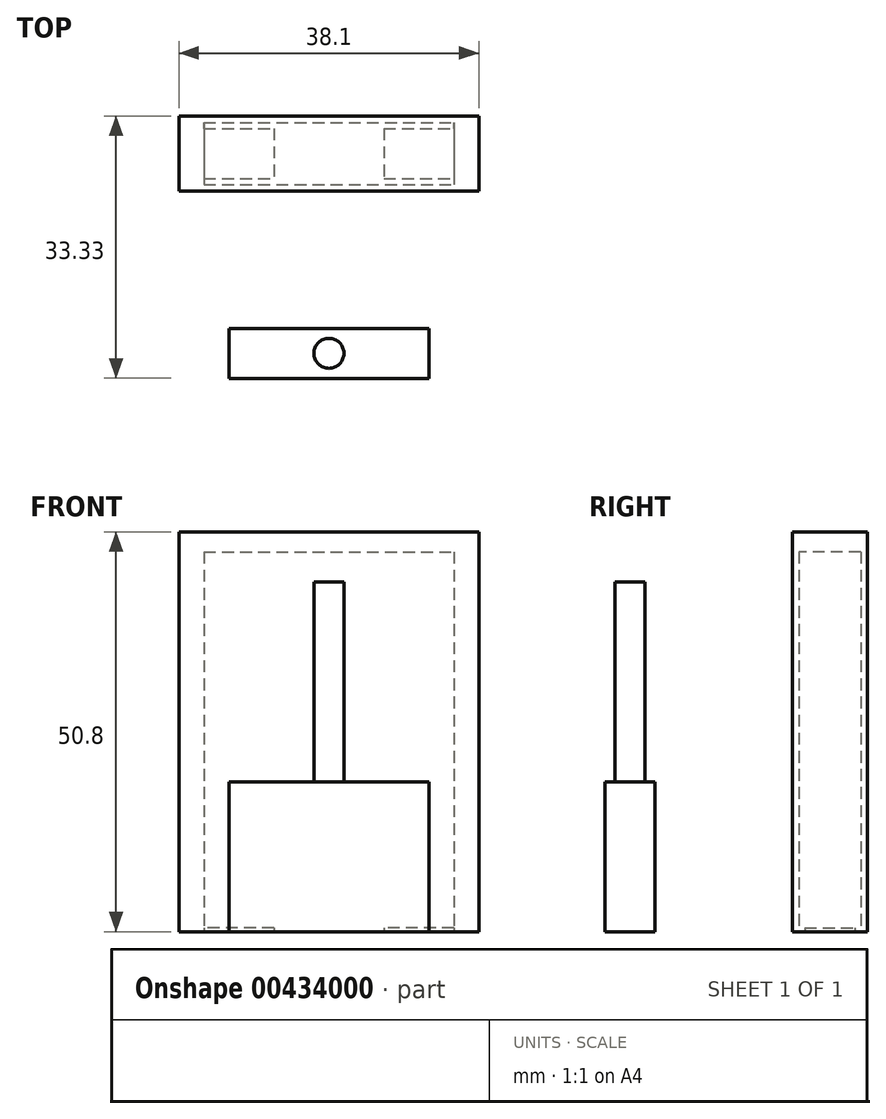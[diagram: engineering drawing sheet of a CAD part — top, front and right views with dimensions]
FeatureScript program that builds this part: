
annotation { "Feature Type Name" : "Feature", "Feature Type Description" : "" }
export const myFeature = defineFeature(function(context is Context, id is Id, definition is map)
    precondition{}
    {
        {
            var Q0;
            Q0=qCreatedBy(makeId("Top.planeOp"),FACE);
            var sketch = newSketch(context, id + "F0", { "sketchPlane" : qUnion([Q0])});
            skLineSegment(sketch, "E0.bottom", {"start": v(19.05, -4.76) * mm, "end": v(-19.05, -4.76) * mm});
            skLineSegment(sketch, "E0.top", {"start": v(19.05, 4.76) * mm, "end": v(-19.05, 4.76) * mm});
            skLineSegment(sketch, "E0.left", {"start": v(19.05, -4.76) * mm, "end": v(19.05, 4.76) * mm});
            skLineSegment(sketch, "E0.right", {"start": v(-19.05, -4.76) * mm, "end": v(-19.05, 4.76) * mm});
            skPoint(sketch, "E0.middle", {"position": v(0, 0) * mm});
            skSolve(sketch);
        }
        {
            var Q0;
            Q0=qCreatedBy(makeId("Top.planeOp"),FACE);
            cPlane(context, id + "F1", {"entities" : qUnion([Q0]), "cplaneType" : CPlaneType.OFFSET, "offset" : 2.54 * mm, "oppositeDirection" : true, "width" : 152.4 * mm, "height" : 152.4 * mm});
        }
        {
            var Q0;
            Q0=qCreatedBy(id+"F1.planeOp",FACE);
            var sketch = newSketch(context, id + "F2", { "sketchPlane" : qUnion([Q0])});
            skLineSegment(sketch, "E1.bottom", {"start": v(15.88, 3.18) * mm, "end": v(-15.88, 3.18) * mm});
            skLineSegment(sketch, "E1.top", {"start": v(15.88, -3.18) * mm, "end": v(-15.88, -3.18) * mm});
            skLineSegment(sketch, "E1.left", {"start": v(15.88, 3.18) * mm, "end": v(15.88, -3.18) * mm});
            skLineSegment(sketch, "E1.right", {"start": v(-15.88, 3.18) * mm, "end": v(-15.88, -3.18) * mm});
            skPoint(sketch, "E1.middle", {"position": v(0, 0) * mm});
            skSolve(sketch);
        }
        {
            var Q0;
            Q0 = qSketchRegion(id + "F0", true);
            extrude(context, id + "F3", {"entities" : qUnion([Q0]), "oppositeDirection" : true, "depth" : 50.8 * mm});
        }
        {
            var Q0;
            Q0 = qSketchRegion(id + "F2", true);
            extrude(context, id + "F4", {"entities" : qUnion([Q0]), "operationType" : NewBodyOperationType.REMOVE, "oppositeDirection" : true, "depth" : 47.75 * mm});
        }
        {
            var Q0;
            Q0=makeQuery(id+"F3.opExtrude","CAP_FACE",FACE,{"disambiguationData":[OSD([sQuery(id+"F0.wireOp",EDGE,"E0.bottom"),sQuery(id+"F0.wireOp",EDGE,"E0.top"),sQuery(id+"F0.wireOp",EDGE,"E0.left"),sQuery(id+"F0.wireOp",EDGE,"E0.right")])],"isStart":false});
            var sketch = newSketch(context, id + "F5", { "sketchPlane" : qUnion([Q0])});
            skLineSegment(sketch, "E2.bottom", {"start": v(6.99, -3.17) * mm, "end": v(-6.99, -3.17) * mm});
            skLineSegment(sketch, "E2.top", {"start": v(6.99, 3.18) * mm, "end": v(-6.99, 3.17) * mm});
            skLineSegment(sketch, "E2.left", {"start": v(6.99, -3.17) * mm, "end": v(6.99, 3.18) * mm});
            skLineSegment(sketch, "E2.right", {"start": v(-6.99, -3.17) * mm, "end": v(-6.99, 3.18) * mm});
            skPoint(sketch, "E2.middle", {"position": v(0, 0) * mm});
            skSolve(sketch);
        }
        {
            var Q0;
            Q0=makeQuery(id+"F5.imprint","IMPRINT",FACE,{"disambiguationData":[TD([[makeQuery(id+"F5.imprint","IMPRINT",EDGE,{"derivedFrom":sQuery(id+"F5.wireOp",EDGE,"E2.bottom")}),-1.0]])]});
            extrude(context, id + "F6", {"entities" : qUnion([Q0]), "operationType" : NewBodyOperationType.REMOVE, "oppositeDirection" : true, "depth" : 25.4 * mm});
        }
        {
            var Q0;
            Q0=makeQuery(id+"F3.opExtrude","CAP_FACE",FACE,{"disambiguationData":[OSD([sQuery(id+"F0.wireOp",EDGE,"E0.bottom"),sQuery(id+"F0.wireOp",EDGE,"E0.top"),sQuery(id+"F0.wireOp",EDGE,"E0.left"),sQuery(id+"F0.wireOp",EDGE,"E0.right")])],"isStart":false});
            var sketch = newSketch(context, id + "F7", { "sketchPlane" : qUnion([Q0])});
            skLineSegment(sketch, "E3.bottom", {"start": v(-15.88, 3.18) * mm, "end": v(15.88, 3.18) * mm});
            skLineSegment(sketch, "E3.top", {"start": v(-15.88, 3.94) * mm, "end": v(15.88, 3.94) * mm});
            skLineSegment(sketch, "E3.left", {"start": v(-15.88, 3.18) * mm, "end": v(-15.88, 3.94) * mm});
            skLineSegment(sketch, "E3.right", {"start": v(15.88, 3.18) * mm, "end": v(15.88, 3.94) * mm});
            skLineSegment(sketch, "E4.bottom", {"start": v(-15.88, -3.18) * mm, "end": v(15.88, -3.18) * mm});
            skLineSegment(sketch, "E4.top", {"start": v(-15.88, -3.94) * mm, "end": v(15.88, -3.94) * mm});
            skLineSegment(sketch, "E4.left", {"start": v(-15.88, -3.17) * mm, "end": v(-15.88, -3.94) * mm});
            skLineSegment(sketch, "E4.right", {"start": v(15.88, -3.17) * mm, "end": v(15.88, -3.94) * mm});
            skSolve(sketch);
        }
        {
            var Q0;
            Q0 = qSketchRegion(id + "F7", true);
            extrude(context, id + "F8", {"entities" : qUnion([Q0]), "operationType" : NewBodyOperationType.REMOVE, "oppositeDirection" : true, "depth" : 48.26 * mm});
        }
        {
            var Q0;
            Q0=qCreatedBy(makeId("Top.planeOp"),FACE);
            cPlane(context, id + "F9", {"entities" : qUnion([Q0]), "cplaneType" : CPlaneType.OFFSET, "offset" : 50.8 * mm, "oppositeDirection" : true, "width" : 152.4 * mm, "height" : 152.4 * mm});
        }
        {
            var Q0;
            Q0=qCreatedBy(id+"F9.planeOp",FACE);
            var sketch = newSketch(context, id + "F10", { "sketchPlane" : qUnion([Q0])});
            skLineSegment(sketch, "E5.bottom", {"start": v(12.7, -28.58) * mm, "end": v(-12.7, -28.58) * mm});
            skLineSegment(sketch, "E5.top", {"start": v(12.7, -22.23) * mm, "end": v(-12.7, -22.23) * mm});
            skLineSegment(sketch, "E5.left", {"start": v(12.7, -28.58) * mm, "end": v(12.7, -22.23) * mm});
            skLineSegment(sketch, "E5.right", {"start": v(-12.7, -28.58) * mm, "end": v(-12.7, -22.23) * mm});
            skPoint(sketch, "E5.middle", {"position": v(0, -25.4) * mm});
            skSolve(sketch);
        }
        {
            var Q0;
            Q0 = qSketchRegion(id + "F10", true);
            extrude(context, id + "F11", {"entities" : qUnion([Q0]), "depth" : 19.05 * mm});
        }
        {
            var Q0;
            Q0=makeQuery(id+"F11.opExtrude","CAP_FACE",FACE,{"disambiguationData":[OSD([sQuery(id+"F10.wireOp",EDGE,"E5.bottom"),sQuery(id+"F10.wireOp",EDGE,"E5.top"),sQuery(id+"F10.wireOp",EDGE,"E5.left"),sQuery(id+"F10.wireOp",EDGE,"E5.right")])],"isStart":false});
            var sketch = newSketch(context, id + "F12", { "sketchPlane" : qUnion([Q0])});
            skLineSegment(sketch, "E6", {"start": v(0, -22.23) * mm, "end": v(0, -28.58) * mm, "construction": true});
            skCircle(sketch, "E7", {"center": v(0, -25.4) * mm, "radius": 1.9 * mm});
            skSolve(sketch);
        }
        {
            var Q0;
            Q0 = qSketchRegion(id + "F12", true);
            var Q1;
            Q1=sQuery(id+"F12.wireOp",EDGE,"E7");
            extrude(context, id + "F13", {"entities" : qUnion([Q0]), "operationType" : NewBodyOperationType.ADD, "surfaceEntities" : qUnion([Q1]), "depth" : 25.4 * mm});
        }
    });
